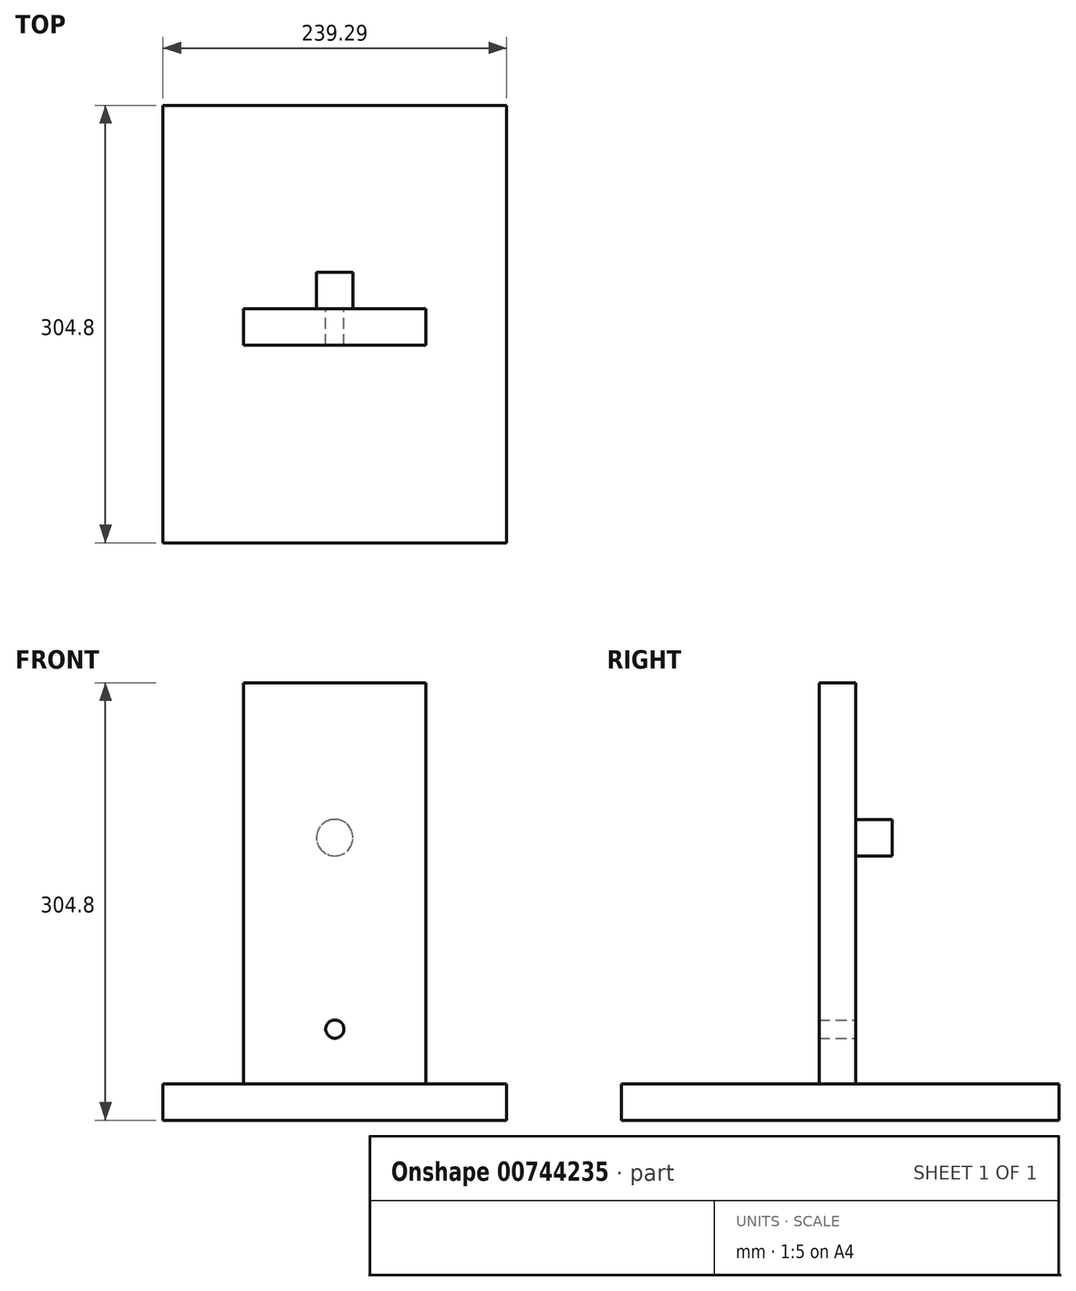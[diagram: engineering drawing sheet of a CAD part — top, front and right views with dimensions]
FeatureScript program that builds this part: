
annotation { "Feature Type Name" : "Feature", "Feature Type Description" : "" }
export const myFeature = defineFeature(function(context is Context, id is Id, definition is map)
    precondition{}
    {
        {
            var Q0;
            Q0=qCreatedBy(makeId("Front.planeOp"),FACE);
            var sketch = newSketch(context, id + "F0", { "sketchPlane" : qUnion([Q0])});
            skLineSegment(sketch, "E0.bottom", {"start": v(-59.93, 185) * mm, "end": v(67.07, 185) * mm});
            skLineSegment(sketch, "E0.top", {"start": v(-59.93, -119.8) * mm, "end": v(67.07, -119.8) * mm});
            skLineSegment(sketch, "E0.left", {"start": v(-59.93, 185) * mm, "end": v(-59.93, -119.8) * mm});
            skLineSegment(sketch, "E0.right", {"start": v(67.07, 185) * mm, "end": v(67.07, -119.8) * mm});
            skPoint(sketch, "E0.middle", {"position": v(3.57, 32.6) * mm});
            skSolve(sketch);
        }
        {
            var Q0;
            Q0=makeQuery(id+"F0.imprint","IMPRINT",FACE,{"disambiguationData":[TD([[makeQuery(id+"F0.imprint","IMPRINT",EDGE,{"derivedFrom":sQuery(id+"F0.wireOp",EDGE,"E0.bottom")}),-1.0]])]});
            extrude(context, id + "F1", {"entities" : qUnion([Q0]), "depth" : 25.4 * mm, "offsetDistance" : 25.4 * mm});
        }
        {
            var Q0;
            Q0=makeQuery(id+"F1.opExtrude","SWEPT_FACE",FACE,{"disambiguationData":[OSD([sQuery(id+"F0.wireOp",EDGE,"E0.top")])]});
            var sketch = newSketch(context, id + "F2", { "sketchPlane" : qUnion([Q0])});
            skLineSegment(sketch, "E1.bottom", {"start": v(123.2, 163.1) * mm, "end": v(-116.08, 163.1) * mm});
            skLineSegment(sketch, "E1.top", {"start": v(123.2, -141.7) * mm, "end": v(-116.08, -141.7) * mm});
            skLineSegment(sketch, "E1.left", {"start": v(123.2, 163.1) * mm, "end": v(123.2, -141.7) * mm});
            skLineSegment(sketch, "E1.right", {"start": v(-116.08, 163.1) * mm, "end": v(-116.08, -141.7) * mm});
            skPoint(sketch, "E1.middle", {"position": v(3.57, 10.7) * mm});
            skPoint(sketch, "E1.middle.positionSnap0", {"position": v(3.57, 25.4) * mm});
            skPoint(sketch, "E1.centerSnap0", {"position": v(3.57, 25.4) * mm});
            skSolve(sketch);
        }
        {
            var Q0;
            Q0=makeQuery(id+"F2.imprint","IMPRINT",FACE,{"disambiguationData":[TD([[makeQuery(id+"F2.imprint","IMPRINT",EDGE,{"derivedFrom":sQuery(id+"F2.wireOp",EDGE,"E1.bottom")}),1.0]])]});
            extrude(context, id + "F3", {"entities" : qUnion([Q0]), "operationType" : NewBodyOperationType.ADD, "oppositeDirection" : true, "depth" : 25.4 * mm, "offsetDistance" : 25.4 * mm});
        }
        {
            var Q0;
            Q0=makeQuery(id+"F1.opExtrude","CAP_FACE",FACE,{"disambiguationData":[OSD([sQuery(id+"F0.wireOp",EDGE,"E0.bottom"),sQuery(id+"F0.wireOp",EDGE,"E0.top"),sQuery(id+"F0.wireOp",EDGE,"E0.left"),sQuery(id+"F0.wireOp",EDGE,"E0.right")])],"isStart":false});
            var sketch = newSketch(context, id + "F4", { "sketchPlane" : qUnion([Q0])});
            skCircle(sketch, "E2", {"center": v(3.57, 77.05) * mm, "radius": 6.35 * mm});
            skLineSegment(sketch, "E3", {"start": v(3.57, 45.3) * mm, "end": v(3.57, 185) * mm, "construction": true});
            skPoint(sketch, "E3.startSnap0", {"position": v(-59.93, 45.3) * mm});
            skPoint(sketch, "E3.startSnap1", {"position": v(3.57, 185) * mm});
            skSolve(sketch);
        }
        {
            var Q0;
            Q0=makeQuery(id+"F4.imprint","IMPRINT",FACE,{"disambiguationData":[TD([[makeQuery(id+"F4.imprint","IMPRINT",EDGE,{"derivedFrom":sQuery(id+"F4.wireOp",EDGE,"E2")}),1.0]])]});
            extrude(context, id + "F5", {"entities" : qUnion([Q0]), "operationType" : NewBodyOperationType.REMOVE, "endBound" : BoundingType.THROUGH_ALL, "oppositeDirection" : true, "depth" : 25.4 * mm, "offsetDistance" : 25.4 * mm});
        }
        {
            var Q0;
            Q0=makeQuery(id+"F1.opExtrude","CAP_FACE",FACE,{"disambiguationData":[OSD([sQuery(id+"F0.wireOp",EDGE,"E0.bottom"),sQuery(id+"F0.wireOp",EDGE,"E0.top"),sQuery(id+"F0.wireOp",EDGE,"E0.left"),sQuery(id+"F0.wireOp",EDGE,"E0.right")])],"isStart":true});
            var sketch = newSketch(context, id + "F6", { "sketchPlane" : qUnion([Q0])});
            skCircle(sketch, "E4", {"center": v(-3.57, 77.05) * mm, "radius": 12.7 * mm});
            skSolve(sketch);
        }
        {
            var Q0;
            Q0=makeQuery(id+"F6.imprint","IMPRINT",FACE,{"disambiguationData":[TD([[makeQuery(id+"F6.imprint","IMPRINT",EDGE,{"derivedFrom":sQuery(id+"F6.wireOp",EDGE,"E4")}),1.0]])]});
            extrude(context, id + "F7", {"entities" : qUnion([Q0]), "operationType" : NewBodyOperationType.REMOVE, "oppositeDirection" : true, "depth" : 32.26 * mm, "offsetDistance" : 25.4 * mm});
        }
        {
            var Q0;
            Q0=makeQuery(id+"F1.opExtrude","CAP_FACE",FACE,{"disambiguationData":[OSD([sQuery(id+"F0.wireOp",EDGE,"E0.bottom"),sQuery(id+"F0.wireOp",EDGE,"E0.top"),sQuery(id+"F0.wireOp",EDGE,"E0.left"),sQuery(id+"F0.wireOp",EDGE,"E0.right")])],"isStart":false});
            var sketch = newSketch(context, id + "F8", { "sketchPlane" : qUnion([Q0])});
            skCircle(sketch, "E5", {"center": v(3.57, 77.05) * mm, "radius": 12.75 * mm});
            skSolve(sketch);
        }
        {
            var Q0;
            Q0=makeQuery(id+"F8.imprint","IMPRINT",FACE,{"disambiguationData":[TD([[makeQuery(id+"F8.imprint","IMPRINT",EDGE,{"derivedFrom":makeQuery(id+"F7.boolean.opBoolean","INTERSECT",EDGE,{"derivedFrom":[makeQuery(id+"F1.opExtrude","CAP_FACE",FACE,{"disambiguationData":[OSD([sQuery(id+"F0.wireOp",EDGE,"E0.bottom"),sQuery(id+"F0.wireOp",EDGE,"E0.top"),sQuery(id+"F0.wireOp",EDGE,"E0.left"),sQuery(id+"F0.wireOp",EDGE,"E0.right")])],"isStart":false}),makeQuery(id+"F7.opExtrude","SWEPT_FACE",FACE,{"disambiguationData":[OSD([sQuery(id+"F6.wireOp",EDGE,"E4")])]})]})}),1.0]])]});
            extrude(context, id + "F9", {"entities" : qUnion([Q0]), "operationType" : NewBodyOperationType.ADD, "oppositeDirection" : true, "depth" : 50.8 * mm, "offsetDistance" : 25.4 * mm});
        }
        {
            var Q0;
            Q0=makeQuery(id+"F1.opExtrude","CAP_FACE",FACE,{"disambiguationData":[OSD([sQuery(id+"F0.wireOp",EDGE,"E0.bottom"),sQuery(id+"F0.wireOp",EDGE,"E0.top"),sQuery(id+"F0.wireOp",EDGE,"E0.left"),sQuery(id+"F0.wireOp",EDGE,"E0.right")])],"isStart":true});
            var sketch = newSketch(context, id + "F10", { "sketchPlane" : qUnion([Q0])});
            skCircle(sketch, "E6", {"center": v(-3.57, -56.3) * mm, "radius": 6.35 * mm});
            skSolve(sketch);
        }
        {
            var Q0;
            Q0=makeQuery(id+"F10.imprint","IMPRINT",FACE,{"disambiguationData":[TD([[makeQuery(id+"F10.imprint","IMPRINT",EDGE,{"derivedFrom":sQuery(id+"F10.wireOp",EDGE,"E6")}),1.0]])]});
            extrude(context, id + "F11", {"entities" : qUnion([Q0]), "operationType" : NewBodyOperationType.REMOVE, "oppositeDirection" : true, "depth" : 78.23 * mm, "offsetDistance" : 25.4 * mm});
        }
    });
